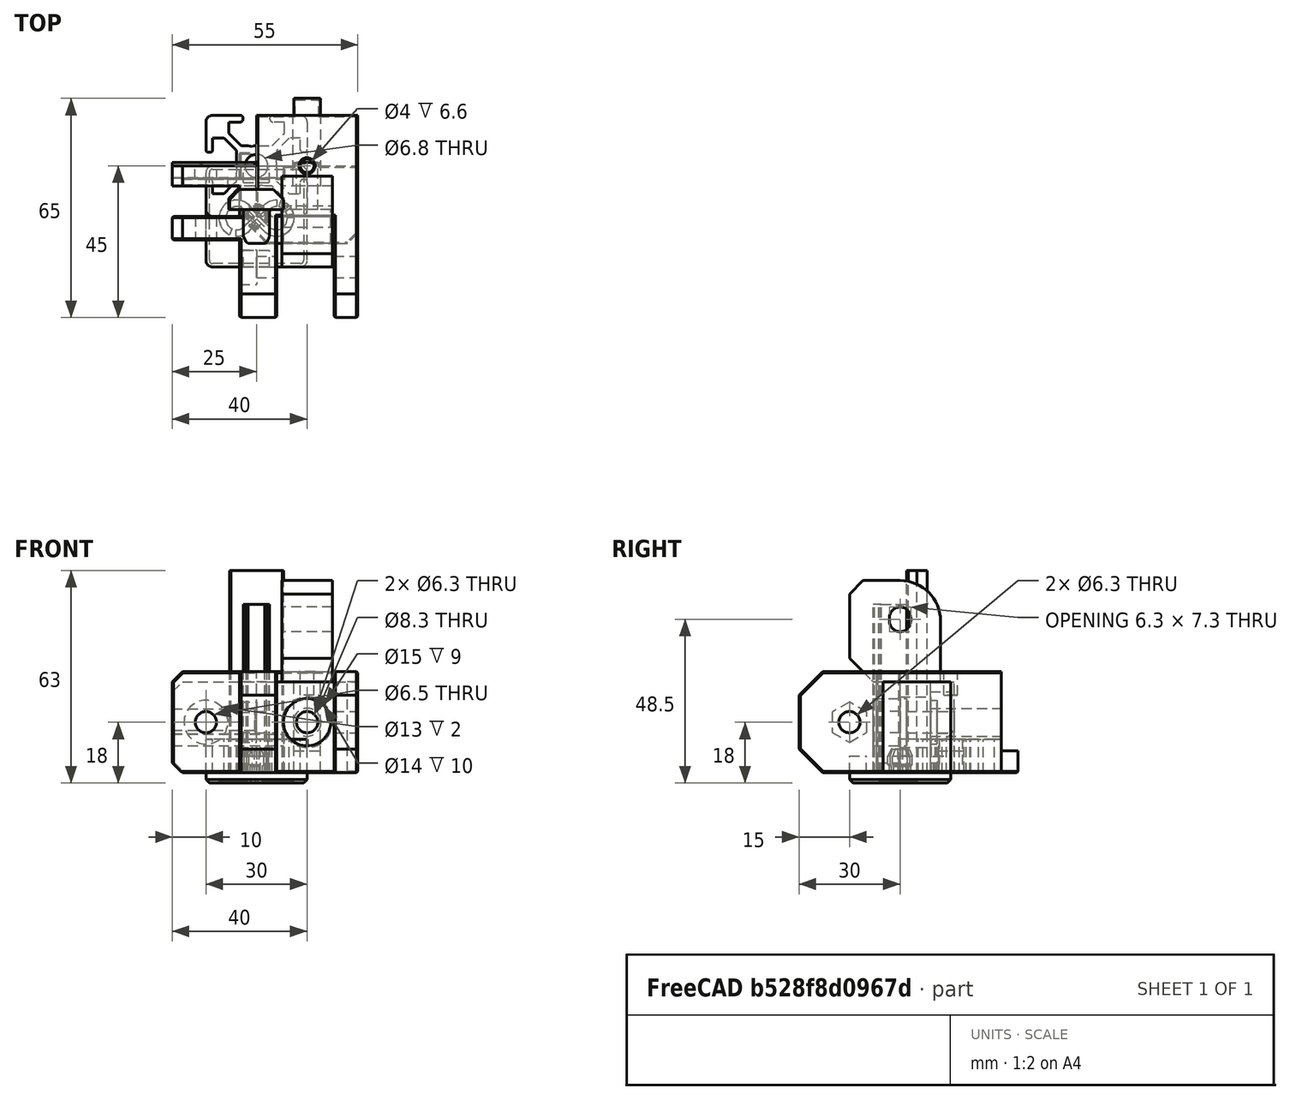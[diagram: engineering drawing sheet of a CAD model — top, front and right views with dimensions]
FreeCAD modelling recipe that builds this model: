
FCSTD DOCUMENT  (FreeCAD 0.19R24291 (Git))
Label: top-lid-hinge
License: Other
LicenseURL: GPL3
objects: Part::Box×20, Part::Chamfer×18, Part::Cylinder×14, Part::MultiFuse×14, Part::Cut×13, Part::Feature×5, Part::Fillet×2, Part::Refine×2, Part::Mirroring×1, Part::Extrusion×1
note: 90 computed .brp shape members not serialized (recipe doc carries the construction recipe); baked Part::Feature solids carry a one-line shape summary decoded from their .brp

FEATURE [Part::Box] Box  label="Cube"
  AttacherType = Attacher::AttachEngine3D
  Height = 30
  Length = 30
  Width = 30
FEATURE [Part::Cylinder] Cylinder
  Angle = 360
  AttacherType = Attacher::AttachEngine3D
  Height = 30
  Placement = pos=(15,3e-15,15) rot=(-1,0,0;1.5708rad)
  Radius = 4.15
FEATURE [Part::Cylinder] Cylinder001
  Angle = 360
  AttacherType = Attacher::AttachEngine3D
  Height = 9
  Placement = pos=(15,3e-15,15) rot=(-1,0,0;1.5708rad)
  Radius = 7.5
FEATURE [Part::Box] Box001  label="Cube001"
  AttacherType = Attacher::AttachEngine3D
  Height = 6.5
  Length = 5
  Placement = pos=(-5,11.1,0) rot=(0,0,1;0rad)
  Width = 7.8
FEATURE [Part::Box] Box002  label="Cube002"
  AttacherType = Attacher::AttachEngine3D
  Height = 6.5
  Length = 7.8
  Placement = pos=(11.1,30,0) rot=(0,0,1;0rad)
  Width = 5
FEATURE [Part::Box] Box003  label="Cube003"
  AttacherType = Attacher::AttachEngine3D
  Height = 30
  Length = 11
  Placement = pos=(-5,-30,0) rot=(0,0,1;0rad)
  Width = 30
FEATURE [Part::Box] Box004  label="Cube004"
  AttacherType = Attacher::AttachEngine3D
  Height = 30
  Length = 7
  Placement = pos=(23,-30,0) rot=(0,0,1;0rad)
  Width = 30
FEATURE [Part::Box] Box005  label="Cube005"
  AttacherType = Attacher::AttachEngine3D
  Height = 30
  Length = 20
  Placement = pos=(-25,-7,0) rot=(0,0,1;0rad)
  Width = 7
FEATURE [Part::Cylinder] Cylinder002
  Angle = 360
  AttacherType = Attacher::AttachEngine3D
  Height = 30
  Placement = pos=(0,-15,15) rot=(0,1,0;1.5708rad)
  Radius = 3.15
FEATURE [Part::Cylinder] Cylinder003
  Angle = 360
  AttacherType = Attacher::AttachEngine3D
  Height = 10
  Placement = pos=(-15,0,15) rot=(1,0,0;1.5708rad)
  Radius = 3.15
FEATURE [Part::Feature] Body001
  Placement = pos=(-5,-15,15) rot=(0,0,1;0rad)
  shape: bbox 5 x 10.31 x 11.9 mm, 8 faces (baked)
FEATURE [Part::MultiFuse] Fusion001
  Shapes = -> [Body001,Cylinder002]
FEATURE [Part::Chamfer] Chamfer001
  Base = -> Box005
  Edges = 2 edges r=3: [Edge2,Edge4]
FEATURE [Part::Cut] Cut002
  Base = -> Chamfer001
  Tool = -> Cylinder003
FEATURE [Part::Box] Box006  label="Cube006"
  AttacherType = Attacher::AttachEngine3D
  Height = 30
  Length = 15
  Placement = pos=(7.5,-15,27) rot=(0,0,1;0rad)
  Width = 27
FEATURE [Part::Box] Box007  label="Cube007"
  AttacherType = Attacher::AttachEngine3D
  Height = 27
  Length = 35
  Placement = pos=(-5,-8,0) rot=(0,0,1;0rad)
  Width = 23
FEATURE [Part::Chamfer] Chamfer002001002
  Base = -> Box006
  Edges = 1 edges r=7: [Edge9]
FEATURE [Part::Fillet] Fillet
  Base = -> Chamfer002001002
  Edges = 1 edges r=12: [Edge11]
FEATURE [Part::Chamfer] Chamfer002001003
  Base = -> Fillet
  Edges = 1 edges r=4: [Edge14]
FEATURE [Part::Box] Box008  label="Cube008"
  AttacherType = Attacher::AttachEngine3D
  Height = 27
  Length = 7.8
  Placement = pos=(11.1,15,0) rot=(0,0,1;0rad)
  Width = 1
FEATURE [Part::Box] Box009  label="Cube009"
  AttacherType = Attacher::AttachEngine3D
  Height = 7.3
  Length = 24.5
  Placement = pos=(-25,14,11.6) rot=(0,0,1;0rad)
  Width = 2
FEATURE [Part::Chamfer] Chamfer002001005
  Base = -> Box007
  Edges = 1 edges r=3: [Edge5]
FEATURE [Part::Chamfer] Chamfer002001006
  Base = -> Chamfer002001005
  Edges = 1 edges r=8: [Edge15]
FEATURE [Part::Cylinder] Cylinder004
  Angle = 360
  AttacherType = Attacher::AttachEngine3D
  Height = 36
  Placement = pos=(15,-15,15) rot=(-1,0,0;1.5708rad)
  Radius = 3.15
FEATURE [Part::Cylinder] Cylinder005
  Angle = 360
  AttacherType = Attacher::AttachEngine3D
  Height = 36
  Placement = pos=(15,-34,15) rot=(-1,0,0;1.5708rad)
  Radius = 7
FEATURE [Part::Cylinder] Cylinder006
  Angle = 360
  AttacherType = Attacher::AttachEngine3D
  Height = 20
  Placement = pos=(0,0,0) rot=(0,-1,0;1.5708rad)
  Radius = 3.15
FEATURE [Part::Cylinder] Cylinder007
  Angle = 360
  AttacherType = Attacher::AttachEngine3D
  Height = 20
  Placement = pos=(2e-16,0,1) rot=(0,-1,0;1.5708rad)
  Radius = 3.15
FEATURE [Part::Box] Box010  label="Cube010"
  AttacherType = Attacher::AttachEngine3D
  Height = 1
  Length = 20
  Placement = pos=(-20,-3.15,0) rot=(0,0,1;0rad)
  Width = 6.3
FEATURE [Part::MultiFuse] Fusion003004
  Placement = pos=(25,0,45) rot=(0,0,1;0rad)
  Shapes = -> [Box010,Cylinder007,Cylinder006]
FEATURE [Part::Cut] Cut004
  Base = -> Chamfer002001003
  Tool = -> Fusion003004
FEATURE [Part::Box] Box011  label="Cube011"
  AttacherType = Attacher::AttachEngine3D
  Height = 8
  Length = 33
  Placement = pos=(-25,11.5,0) rot=(0,0,1;0rad)
  Width = 3.5
FEATURE [Part::MultiFuse] Fusion003008
  Shapes = -> [Cylinder005,Cylinder004]
FEATURE [Part::Box] Box012  label="Cube012"
  AttacherType = Attacher::AttachEngine3D
  Height = 27
  Length = 20
  Placement = pos=(-25,9,0) rot=(0,0,1;0rad)
  Width = 6
FEATURE [Part::Chamfer] Chamfer002001007
  Base = -> Box012
  Edges = 2 edges r=3: [Edge2,Edge4]
FEATURE [Part::Chamfer] Chamfer002001008
  Base = -> Box009
  Edges = 1 edges r=1: [Edge11]
FEATURE [Part::MultiFuse] Fusion003009
  Shapes = -> [Chamfer002001006,Chamfer002001007]
FEATURE [Part::Cut] Cut005
  Base = -> Fusion003009
  Tool = -> Box011
FEATURE [Part::Chamfer] Chamfer002001009
  Base = -> Cut005
  Edges = 1 edges r=3.49: [Edge24]
FEATURE [Part::MultiFuse] Fusion003010
  Shapes = -> [Chamfer002001008,Box008]
FEATURE [Part::MultiFuse] Fusion003011
  Shapes = -> [Chamfer002001009,Fusion003010]
FEATURE [Part::Cut] Cut006
  Base = -> Fusion003011
  Tool = -> Fusion003008
FEATURE [Part::Cylinder] Cylinder008
  Angle = 360
  AttacherType = Attacher::AttachEngine3D
  Height = 19
  Placement = pos=(-15,3e-15,15) rot=(-1,0,0;1.5708rad)
  Radius = 3.25
FEATURE [Part::Cylinder] Cylinder009
  Angle = 360
  AttacherType = Attacher::AttachEngine3D
  Height = 19
  Placement = pos=(-15,-8,15) rot=(-1,0,0;1.5708rad)
  Radius = 6.5
FEATURE [Part::Cut] Cut007
  Base = -> Cut006
  Tool = -> Cylinder008
FEATURE [Part::Cut] Cut008
  Base = -> Cut007
  Tool = -> Cylinder009
FEATURE [Part::MultiFuse] Fusion003012
  Shapes = -> [Cut008,Cut004]
FEATURE [Part::Refine] Fusion003012001
  Source = -> Fusion003012
FEATURE [Part::Chamfer] Chamfer002001010
  Base = -> Fusion003012001
  Edges = 13 edges r=0.4: [Edge31,Edge37,Edge43,Edge50,Edge55,Edge56,Edge59,Edge64,Edge68,Edge74,Edge78,Edge79,Edge116]
FEATURE [Part::MultiFuse] Fusion
  Shapes = -> [Cylinder001,Cylinder]
FEATURE [Part::Cut] Cut
  Base = -> Box
  Tool = -> Fusion
FEATURE [Part::MultiFuse] Fusion003012002
  Shapes = -> [Box004,Box003]
FEATURE [Part::Chamfer] Chamfer
  Base = -> Fusion003012002
  Edges = 4 edges r=7: [Edge9,Edge10,Edge21,Edge22]
FEATURE [Part::Cut] Cut009
  Base = -> Chamfer
  Tool = -> Fusion001
FEATURE [Part::MultiFuse] Fusion003012003
  Shapes = -> [Cut009,Cut,Cut002,Box002,Box001]
FEATURE [Part::Refine] Fusion003012003001
  Source = -> Fusion003012003
FEATURE [Part::Chamfer] Chamfer002001011
  Base = -> Fusion003012003001
  Edges = 42 edges r=0.4: [Edge1,Edge2,Edge3,Edge4,Edge5,Edge8,Edge11,Edge13,Edge15,Edge16,Edge21,Edge22,Edge23,Edge24,Edge25,Edge30,Edge32,Edge34,Edge41,Edge43,Edge47,Edge49,Edge53,Edge56,Edge61,Edge63,Edge66,Edge70,Edge71,Edge72,Edge74,Edge87,Edge89,Edge90,Edge91,Edge100,Edge103,Edge105,Edge108,Edge109,Edge110,Edge111]
FEATURE [Part::Cylinder] Cylinder010
  Angle = 360
  AttacherType = Attacher::AttachEngine3D
  Height = 10
  Placement = pos=(15,15,23) rot=(0,0,1;0rad)
  Radius = 2
FEATURE [Part::Cut] Cut010
  Base = -> Chamfer002001011
  Tool = -> Cylinder010
FEATURE [Part::Chamfer] Chamfer002001012
  Base = -> Cut010
  Edges = 1 edges r=0.4: [Edge47]
FEATURE [Part::Box] Box013  label="Cube013"
  AttacherType = Attacher::AttachEngine3D
  Height = 3
  Length = 30
  Placement = pos=(-15,-15,-3) rot=(0,0,1;0rad)
  Width = 30
FEATURE [Part::Cylinder] Cylinder011
  Angle = 360
  AttacherType = Attacher::AttachEngine3D
  Height = 7
  Radius = 3.65
FEATURE [Part::Box] Box014  label="Cube014"
  AttacherType = Attacher::AttachEngine3D
  Height = 5
  Length = 7.8
  Placement = pos=(-3.9,10,0) rot=(0,0,1;0rad)
  Width = 5
FEATURE [Part::Box] Box015  label="Cube015"
  AttacherType = Attacher::AttachEngine3D
  Height = 5
  Length = 7.8
  Placement = pos=(-3.9,-15,0) rot=(0,0,1;0rad)
  Width = 5
FEATURE [Part::Fillet] Fillet001
  Base = -> Box013
  Edges = 4 edges r=2: [Edge1,Edge3,Edge5,Edge7]
FEATURE [Part::Feature] snakeoil_logo_1_001001_solid  label="snakeoil_logo_1_001001 (Solid)"
  Placement = pos=(-67,-27,-25) rot=(0,0,1;0rad)
  shape: bbox 30 x 30 x 23 mm, 327 faces (baked)
FEATURE [Part::Mirroring] Part__Mirroring  label="snakeoil_logo_1_001001 (Solid) (Mirror #1)"
  Base = (0,0,0)
  Normal = (1,0,0)
  Source = -> snakeoil_logo_1_001001_solid
FEATURE [Part::Chamfer] Chamfer002001015
  Base = -> Fillet001
  Edges = 8 edges r=1: [Edge3,Edge12,Edge14,Edge16,Edge17,Edge18,Edge19,Edge20]
FEATURE [Part::Feature] Part__Feature_cs  label="profile-template"
  Placement = pos=(0,0,-1) rot=(0,0,1;0rad)
  shape: bbox 30 x 30 x 3e-07 mm, 0 faces, 0 solids (baked)
FEATURE [Part::Extrusion] Extrude
  Base = -> Part__Feature_cs
  Dir = (0,0,1)
  DirMode = 2
  FaceMakerClass = Part::FaceMakerBullseye
  LengthFwd = 10
  LengthRev = 0
  Placement = pos=(0,15,0) rot=(0,0,1;0rad)
  Solid = true
  Symmetric = false
FEATURE [Part::Box] Box016  label="Cube016"
  AttacherType = Attacher::AttachEngine3D
  Height = 60
  Length = 16
  Placement = pos=(-8,2,0) rot=(0,0,1;0rad)
  Width = 6
FEATURE [Part::Box] Box017  label="Cube017"
  AttacherType = Attacher::AttachEngine3D
  Height = 50
  Length = 7.8
  Placement = pos=(-3.9,-8,0) rot=(0,0,1;0rad)
  Width = 10
FEATURE [Part::Chamfer] Chamfer002001016
  Base = -> Box016
  Edges = 2 edges r=3: [Edge3,Edge7]
FEATURE [Part::Chamfer] Chamfer002001017
  Base = -> Box017
  Edges = 2 edges: [Edge1 r1=2 r2=1,Edge5 r1=2 r2=1]
FEATURE [Part::MultiFuse] Fusion003012003003
  Shapes = -> [Chamfer002001017,Chamfer002001016]
FEATURE [Part::Chamfer] Chamfer002001018
  Base = -> Fusion003012003003
  Edges = 5 edges r=0.4: [Edge2,Edge15,Edge31,Edge36,Edge37]
FEATURE [Part::Feature] Chamfer002001018001001001
  shape: bbox 16 x 16 x 60 mm, 19 faces (baked)
FEATURE [Part::Cylinder] Cylinder012
  Angle = 360
  AttacherType = Attacher::AttachEngine3D
  Height = 10
  Radius = 3.15
FEATURE [Part::Cylinder] Cylinder013
  Angle = 360
  AttacherType = Attacher::AttachEngine3D
  Height = 2
  Radius = 5
FEATURE [Part::Box] Box018  label="Cube018"
  AttacherType = Attacher::AttachEngine3D
  Height = 10
  Length = 10
  Placement = pos=(-5,-0.5,0) rot=(0,0,1;0rad)
  Width = 1
FEATURE [Part::Box] Box019  label="Cube019"
  AttacherType = Attacher::AttachEngine3D
  Height = 10
  Length = 10
  Placement = pos=(0.5,-4.5,0) rot=(0,0,1;1.5708rad)
  Width = 1
FEATURE [Part::MultiFuse] Fusion003012003004
  Placement = pos=(0,0,0) rot=(0,0,-1;0.785398rad)
  Shapes = -> [Box019,Box018]
FEATURE [Part::Chamfer] Chamfer002001018001001002
  Base = -> Cylinder011
  Edges = 1 edges: [Edge1 r1=2 r2=1]
FEATURE [Part::Cut] Cut011
  Base = -> Cylinder013
  Tool = -> Cylinder012
FEATURE [Part::Cut] Cut012
  Base = -> Chamfer002001018001001002
  Tool = -> Cut011
FEATURE [Part::Chamfer] Chamfer002001018001001003
  Base = -> Cut012
  Edges = 1 edges r=0.49: [Edge1]
FEATURE [Part::Cut] Cut013
  Base = -> Chamfer002001018001001003
  Tool = -> Fusion003012003004
FEATURE [Part::MultiFuse] Fusion003012003005
  Shapes = -> [Box014,Cut013,Box015]
FEATURE [Part::Cut] Cut014
  Base = -> Chamfer002001015
  Tool = -> Part__Mirroring
FEATURE [Part::MultiFuse] Fusion003012003006
  Shapes = -> [Cut014,Fusion003012003005]
FEATURE [Part::Feature] Fusion003012003006001
  shape: bbox 30 x 30 x 10 mm, 385 faces (baked)
